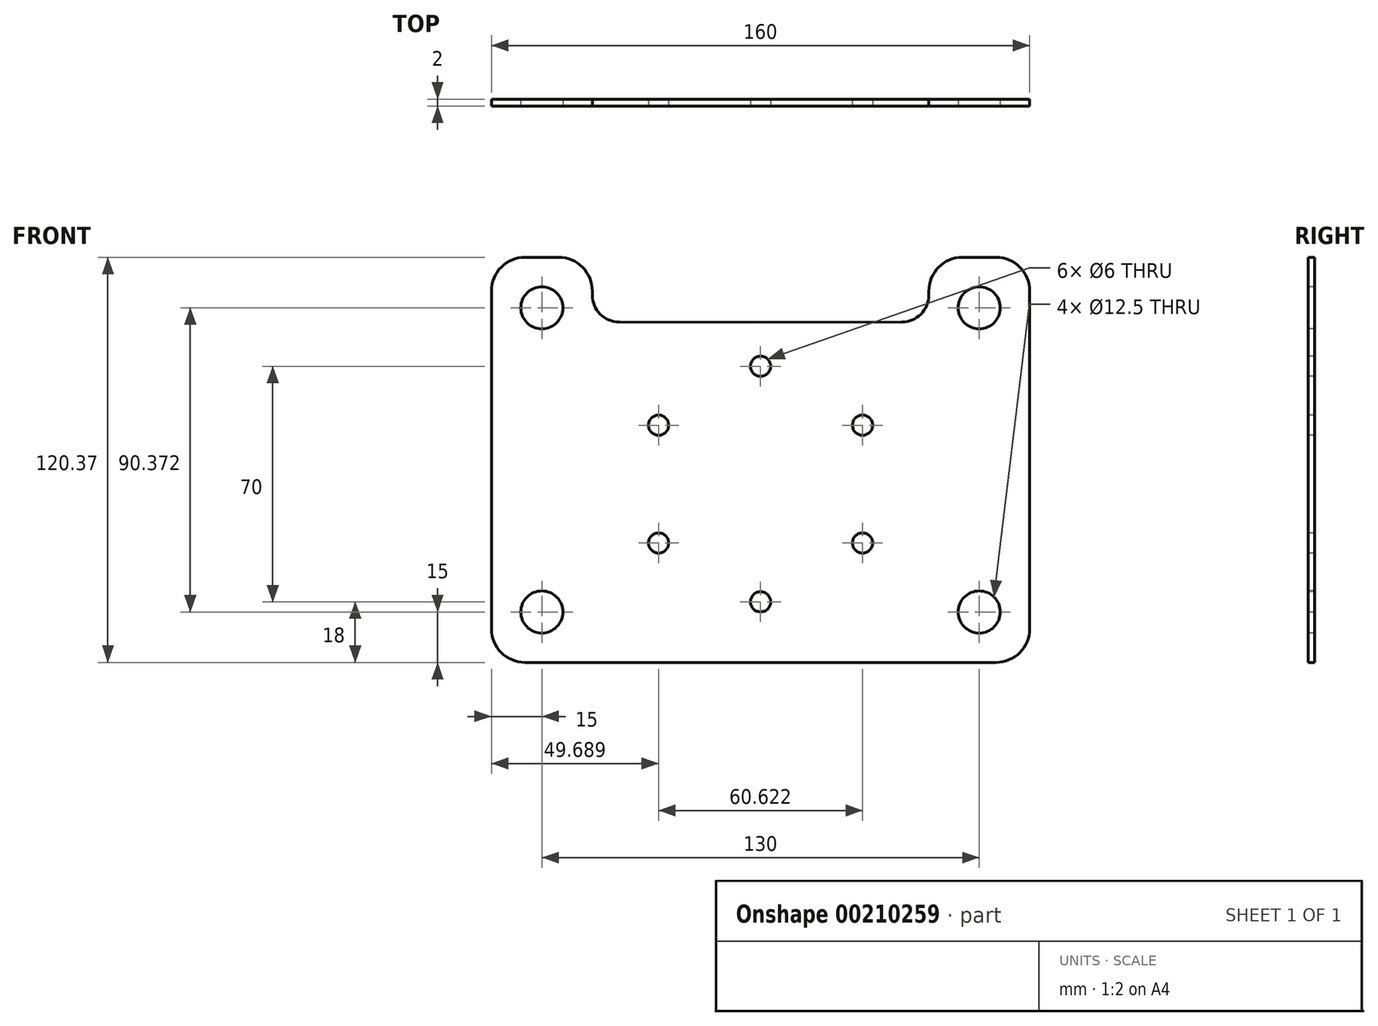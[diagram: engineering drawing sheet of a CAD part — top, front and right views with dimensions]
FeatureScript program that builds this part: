
annotation { "Feature Type Name" : "Feature", "Feature Type Description" : "" }
export const myFeature = defineFeature(function(context is Context, id is Id, definition is map)
    precondition{}
    {
        {
            var Q0;
            Q0=qCreatedBy(makeId("Front.planeOp"),FACE);
            var sketch = newSketch(context, id + "F0", { "sketchPlane" : qUnion([Q0])});
            skCircle(sketch, "E0", {"center": v(0, 0) * mm, "radius": 27.5 * mm});
            skCircle(sketch, "E1", {"center": v(0, 35) * mm, "radius": 3 * mm});
            skCircle(sketch, "E2.1.0", {"center": v(-30.31, 17.5) * mm, "radius": 3 * mm});
            skCircle(sketch, "E2.2.0", {"center": v(-30.31, -17.5) * mm, "radius": 3 * mm});
            skCircle(sketch, "E2.3.0", {"center": v(0, -35) * mm, "radius": 3 * mm});
            skCircle(sketch, "E2.4.0", {"center": v(30.31, -17.5) * mm, "radius": 3 * mm});
            skCircle(sketch, "E2.5.0", {"center": v(30.31, 17.5) * mm, "radius": 3 * mm});
            skLineSegment(sketch, "E3", {"start": v(0, -80) * mm, "end": v(-18, -80) * mm});
            skArc(sketch, "E4", {"start": v(-37.9, -38.47) * mm, "mid": v(-59.22, -23.35) * mm, "end": v(-84, -15) * mm});
            skArc(sketch, "E5", {"start": v(-18, -80) * mm, "mid": v(-25.25, -57.94) * mm, "end": v(-37.9, -38.47) * mm});
            skLineSegment(sketch, "E6", {"start": v(-84, 30) * mm, "end": v(-84, -15) * mm});
            skArc(sketch, "E7", {"start": v(0, 48) * mm, "mid": v(-43.03, 43.8) * mm, "end": v(-84, 30) * mm});
            skArc(sketch, "E8.MirrorCS", {"start": v(0, 48) * mm, "mid": v(43.03, 43.8) * mm, "end": v(84, 30) * mm});
            skLineSegment(sketch, "E9.MirrorCS", {"start": v(84, 30) * mm, "end": v(84, -15) * mm});
            skLineSegment(sketch, "E10.MirrorCS", {"start": v(84, -15) * mm, "end": v(84, -15) * mm});
            skArc(sketch, "E11.MirrorCS", {"start": v(37.9, -38.47) * mm, "mid": v(59.22, -23.35) * mm, "end": v(84, -15) * mm});
            skArc(sketch, "E12.MirrorCS", {"start": v(18, -80) * mm, "mid": v(25.25, -57.94) * mm, "end": v(37.9, -38.47) * mm});
            skLineSegment(sketch, "E13.MirrorCS", {"start": v(0, -80) * mm, "end": v(18, -80) * mm});
            skLineSegment(sketch, "E14", {"start": v(0, 0) * mm, "end": v(37.9, -38.47) * mm});
            skSolve(sketch);
        }
        {
            var Q0;
            Q0=qCreatedBy(makeId("Front.planeOp"),FACE);
            var sketch = newSketch(context, id + "F1", { "sketchPlane" : qUnion([Q0])});
            skCircle(sketch, "E15", {"center": v(-65, 52.37) * mm, "radius": 6.25 * mm});
            skPoint(sketch, "E16.center", {"position": v(0, 0) * mm});
            skArc(sketch, "E17.filletArc", {"start": v(-70, 67.37) * mm, "mid": v(-77.07, 64.44) * mm, "end": v(-80, 57.37) * mm});
            skLineSegment(sketch, "E18", {"start": v(0, 35) * mm, "end": v(0, 48) * mm});
            skCircle(sketch, "E19", {"center": v(0, 35) * mm, "radius": 3 * mm});
            skLineSegment(sketch, "E20", {"start": v(-80, 57.37) * mm, "end": v(-80, 0) * mm});
            skLineSegment(sketch, "E21", {"start": v(-70, 67.37) * mm, "end": v(-60, 67.37) * mm});
            skLineSegment(sketch, "E22", {"start": v(-50, 57.37) * mm, "end": v(-50, 56.15) * mm});
            skLineSegment(sketch, "E23", {"start": v(0, 48) * mm, "end": v(-42.03, 48.15) * mm});
            skPoint(sketch, "E24.visualSharp", {"position": v(-50, 67.37) * mm});
            skArc(sketch, "E24.filletArc", {"start": v(-50, 57.37) * mm, "mid": v(-52.93, 64.44) * mm, "end": v(-60, 67.37) * mm});
            skPoint(sketch, "E25.visualSharp", {"position": v(-50, 48.18) * mm});
            skArc(sketch, "E25.filletArc", {"start": v(-50, 56.15) * mm, "mid": v(-47.67, 50.5) * mm, "end": v(-42.03, 48.15) * mm});
            skLineSegment(sketch, "E26.MirrorCS", {"start": v(0, 48) * mm, "end": v(42.03, 48.15) * mm});
            skArc(sketch, "E27.MirrorCS", {"start": v(50, 56.15) * mm, "mid": v(47.67, 50.5) * mm, "end": v(42.03, 48.15) * mm});
            skArc(sketch, "E28.MirrorCS", {"start": v(50, 57.37) * mm, "mid": v(52.93, 64.44) * mm, "end": v(60, 67.37) * mm});
            skLineSegment(sketch, "E29.MirrorCS", {"start": v(70, 67.37) * mm, "end": v(60, 67.37) * mm});
            skCircle(sketch, "E30.MirrorC", {"center": v(65, 52.37) * mm, "radius": 6.25 * mm});
            skArc(sketch, "E31.MirrorCS", {"start": v(70, 67.37) * mm, "mid": v(77.07, 64.44) * mm, "end": v(80, 57.37) * mm});
            skLineSegment(sketch, "E32.MirrorCS", {"start": v(80, 57.37) * mm, "end": v(80, 0) * mm});
            skLineSegment(sketch, "E33.MirrorCS", {"start": v(50, 57.37) * mm, "end": v(50, 56.15) * mm});
            skCircle(sketch, "E34", {"center": v(-65, -38) * mm, "radius": 6.25 * mm});
            skLineSegment(sketch, "E35", {"start": v(0, -53) * mm, "end": v(-70, -53) * mm});
            skLineSegment(sketch, "E36", {"start": v(-80, -43) * mm, "end": v(-80, 0) * mm});
            skPoint(sketch, "E37.visualSharp", {"position": v(-80, -53) * mm});
            skArc(sketch, "E37.filletArc", {"start": v(-80, -43) * mm, "mid": v(-77.07, -50.07) * mm, "end": v(-70, -53) * mm});
            skLineSegment(sketch, "E38.MirrorCS", {"start": v(0, -53) * mm, "end": v(70, -53) * mm});
            skArc(sketch, "E39.MirrorCS", {"start": v(80, -43) * mm, "mid": v(77.07, -50.07) * mm, "end": v(70, -53) * mm});
            skLineSegment(sketch, "E40.MirrorCS", {"start": v(80, -43) * mm, "end": v(80, 0) * mm});
            skCircle(sketch, "E41.MirrorC", {"center": v(65, -38) * mm, "radius": 6.25 * mm});
            skCircle(sketch, "E42.1.0", {"center": v(-30.31, 17.5) * mm, "radius": 3 * mm});
            skCircle(sketch, "E42.2.0", {"center": v(-30.31, -17.5) * mm, "radius": 3 * mm});
            skCircle(sketch, "E42.3.0", {"center": v(0, -35) * mm, "radius": 3 * mm});
            skCircle(sketch, "E42.4.0", {"center": v(30.31, -17.5) * mm, "radius": 3 * mm});
            skCircle(sketch, "E42.5.0", {"center": v(30.31, 17.5) * mm, "radius": 3 * mm});
            skSolve(sketch);
        }
        {
            var Q0;
            Q0=makeQuery(id+"F1.imprint","IMPRINT",FACE,{"disambiguationData":[TD([[makeQuery(id+"F1.imprint","IMPRINT",EDGE,{"derivedFrom":sQuery(id+"F1.wireOp",EDGE,"E15")}),-1.0]])]});
            extrude(context, id + "F2", {"entities" : qUnion([Q0]), "oppositeDirection" : true, "depth" : 2 * mm});
        }
    });
